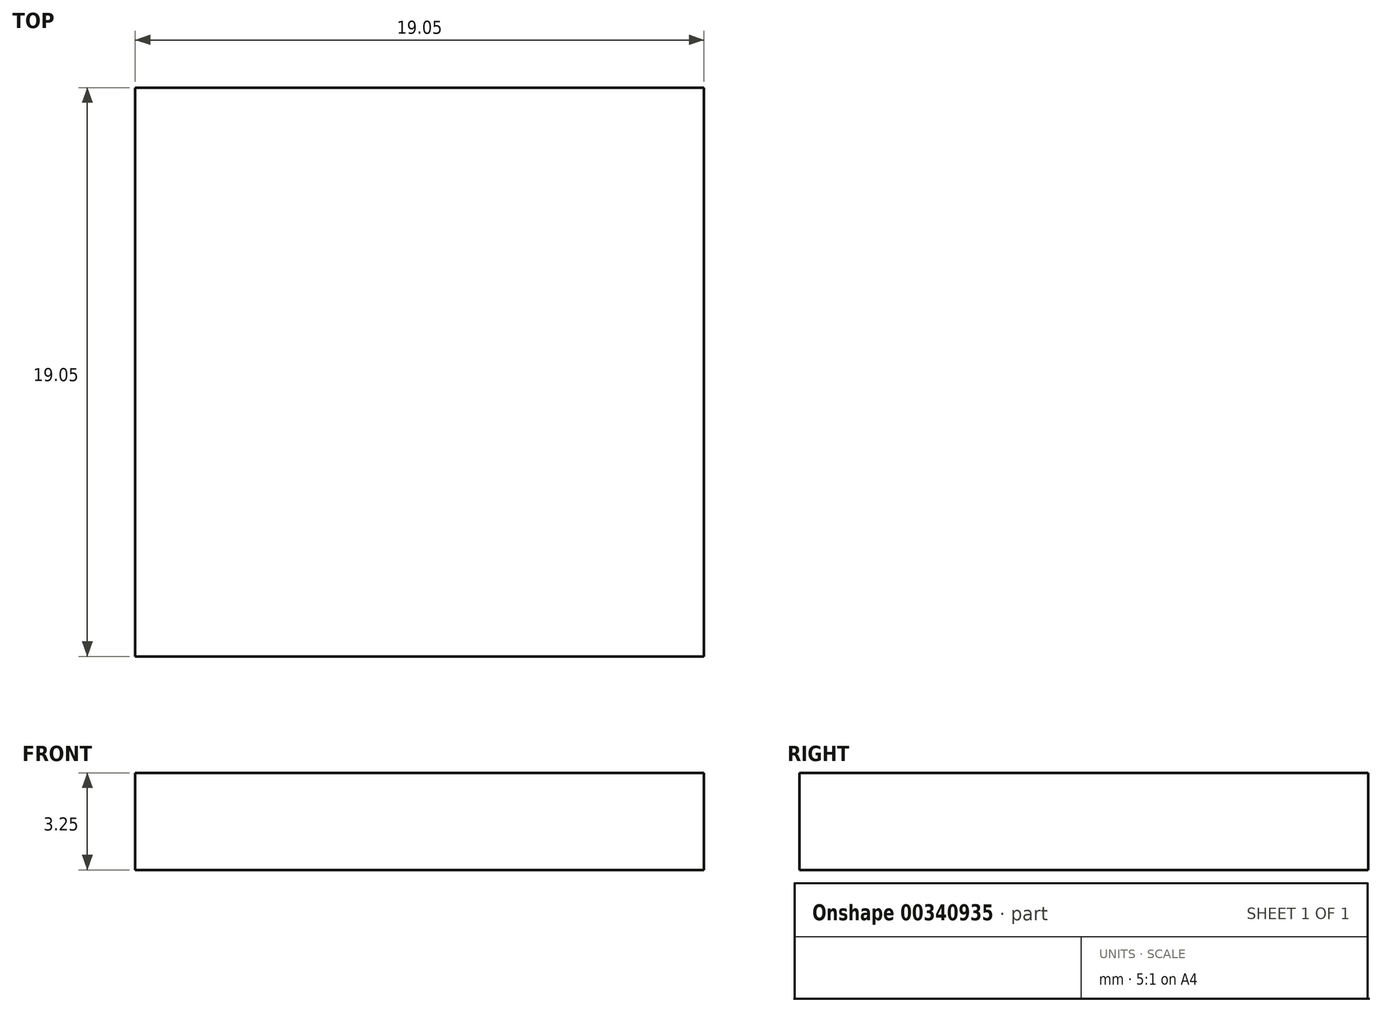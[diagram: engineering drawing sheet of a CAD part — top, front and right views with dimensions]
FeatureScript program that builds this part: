
annotation { "Feature Type Name" : "Feature", "Feature Type Description" : "" }
export const myFeature = defineFeature(function(context is Context, id is Id, definition is map)
    precondition{}
    {
        {
            var Q0;
            Q0=qCreatedBy(makeId("Top.planeOp"),FACE);
            var sketch = newSketch(context, id + "F0", { "sketchPlane" : qUnion([Q0])});
            skLineSegment(sketch, "E0.bottom", {"start": v(0, 0) * mm, "end": v(19.05, 0) * mm});
            skLineSegment(sketch, "E0.top", {"start": v(0, -19.05) * mm, "end": v(19.05, -19.05) * mm});
            skLineSegment(sketch, "E0.left", {"start": v(0, 0) * mm, "end": v(0, -19.05) * mm});
            skLineSegment(sketch, "E0.right", {"start": v(19.05, 0) * mm, "end": v(19.05, -19.05) * mm});
            skSolve(sketch);
        }
        {
            var Q0;
            Q0 = qSketchRegion(id + "F0", true);
            extrude(context, id + "F1", {"entities" : qUnion([Q0]), "depth" : 3.25 * mm});
        }
    });
